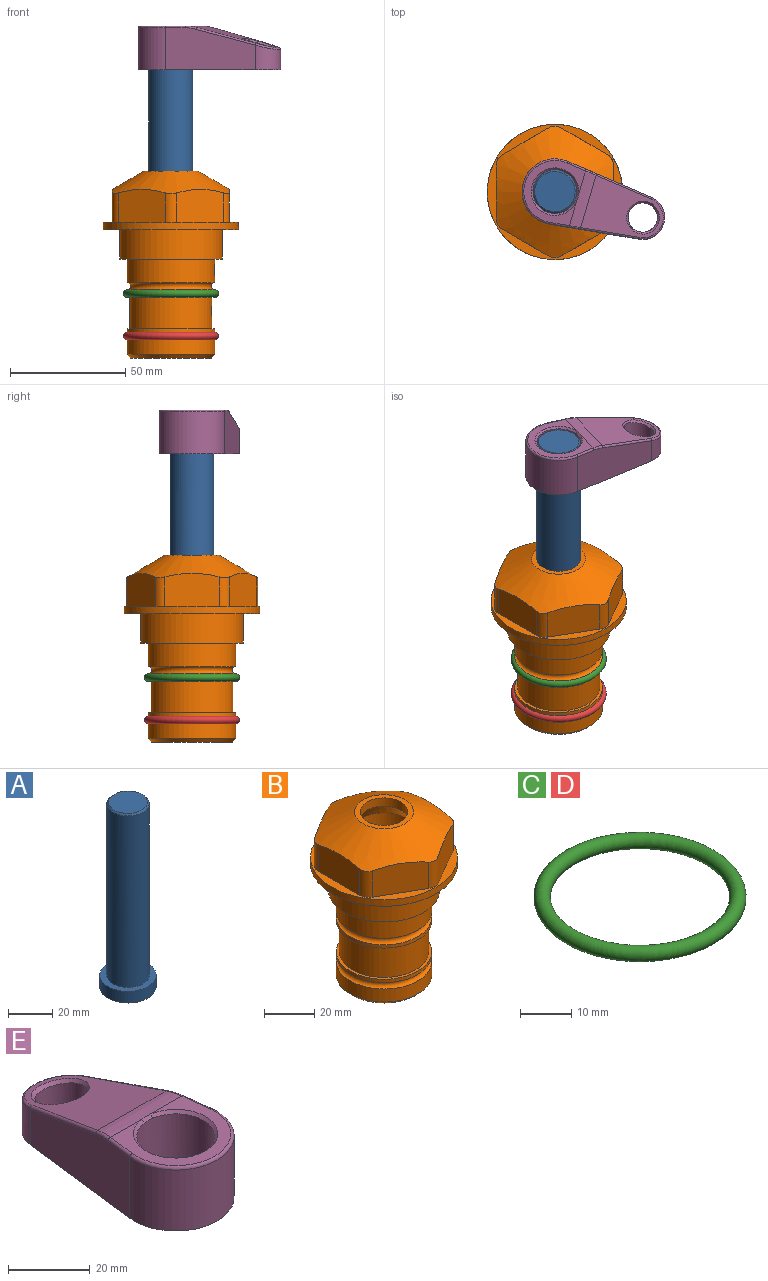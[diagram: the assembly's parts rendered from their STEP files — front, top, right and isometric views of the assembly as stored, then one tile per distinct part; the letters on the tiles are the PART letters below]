
ASSEMBLY  parts=5 mates=4
PART A: 6 faces, bbox 25.4x25.4x101.6 mm
  f0: plane 17.46x17.46mm, normal (0,0,1), area 239.5mm2, adj f5
  f1: plane 25.4x25.4mm, normal (0,0,-1), area 506.7mm2, adj f2
  f2: cylinder r=12.7mm len=25.4mm, axis (0,0,1), area 506.7mm2, adj f1,f3
  f3: plane 25.4x25.4mm, normal (0,0,1), area 221.7mm2, adj f2,f4
  f4: cylinder r=9.53mm len=94.46mm, axis (0,0,1), area 5653mm2, adj f3,f5
  f5: cone r=8.73mm half-angle=45deg, axis (0,0,-1), area 64.4mm2, adj f0,f4
PART B: 36 faces, bbox 58.7x58.7x81 mm
  f0: cylinder r=17.78mm len=35.56mm, axis (0,0,1), area 1670.8mm2, adj f23,f24,f31
  f1: cylinder r=19.05mm len=38.1mm, axis (0,0,1), area 1191.9mm2, adj f26,f27,f30
  f2: plane 58.66x58.66mm, normal (0,0,-1), area 1150.6mm2, adj f3,f28
  f3: cylinder r=29.33mm len=58.66mm, axis (0,0,-1), area 585.1mm2, adj f2,f4
  f4: plane 58.66x58.66mm, normal (0,0,1), area 475.9mm2, adj f3,f5,f6,f7,f8,f9,f10,f11
  f5: plane 20.32x14.34mm, normal (-0.5,0.87,0), area 324.4mm2, adj f4,f15,f16,f17
  f6: plane 20.32x14.34mm, normal (0.5,0.87,0), area 324.4mm2, adj f4,f14,f15,f17
  f7: plane 23.48x14.34mm, normal (1,0,0), area 324.4mm2, adj f4,f13,f14,f17
  f8: plane 20.32x14.34mm, normal (0.5,-0.87,0), area 324.4mm2, adj f4,f12,f13,f17
  f9: plane 20.32x14.34mm, normal (-0.5,-0.87,0), area 324.4mm2, adj f4,f11,f12,f17
  f10: plane 23.48x14.34mm, normal (-1,0,0), area 324.4mm2, adj f4,f11,f16,f17
  f11: cylinder r=5.08mm len=12.85mm, axis (0,0,-1), area 67.2mm2, adj f4,f9,f10,f17
  f12: cylinder r=5.08mm len=12.85mm, axis (0,0,-1), area 67.2mm2, adj f4,f8,f9,f17
  f13: cylinder r=5.08mm len=12.85mm, axis (0,0,-1), area 67.2mm2, adj f4,f7,f8,f17
  f14: cylinder r=5.08mm len=12.85mm, axis (0,0,-1), area 67.2mm2, adj f4,f6,f7,f17
  f15: cylinder r=5.08mm len=12.85mm, axis (0,0,-1), area 67.2mm2, adj f4,f5,f6,f17
  f16: cylinder r=5.08mm len=12.85mm, axis (0,0,-1), area 67.2mm2, adj f4,f5,f10,f17
  f17: cone r=11.73mm half-angle=60deg, axis (0,0,-1), area 2071.8mm2, adj f5,f6,f7,f8,f9,f10,f11,f12
  f18: plane 23.46x23.46mm, normal (0,0,1), area 147.4mm2, adj f17,f35
  f19: plane 34.93x34.93mm, normal (0,0,-1), area 958mm2, adj f29
  f20: cylinder r=19.05mm len=38.1mm, axis (0,0,1), area 760.1mm2, adj f21,f29
  f21: torus R=19.05mm, axis (0,0,1), area 565.3mm2, adj f20,f22
  f22: cylinder r=19.05mm len=38.1mm, axis (0,0,1), area 190mm2, adj f21,f23
  f23: plane 38.1x38.1mm, normal (0,0,1), area 146.9mm2, adj f0,f22
  f24: plane 38.1x38.1mm, normal (0,0,-1), area 146.9mm2, adj f0,f25
  f25: cylinder r=19.05mm len=38.1mm, axis (0,0,1), area 190mm2, adj f24,f26
  f26: torus R=19.05mm, axis (0,0,1), area 565.3mm2, adj f1,f25
  f27: plane 44.45x44.45mm, normal (0,0,-1), area 411.7mm2, adj f1,f28
  f28: cylinder r=22.23mm len=44.45mm, axis (0,0,1), area 1773.5mm2, adj f2,f27
  f29: cone r=19.05mm half-angle=45deg, axis (0,0,1), area 257.5mm2, adj f19,f20
  f30: cylinder r=3.17mm len=6.75mm, axis (-1,0,0), area 128mm2, adj f1,f33
  f31: cylinder r=3.17mm len=6.35mm, axis (-1,0,0), area 102.5mm2, adj f0,f33
  f32: plane 25.4x25.4mm, normal (0,0,1), area 506.7mm2, adj f33
  f33: cylinder r=12.7mm len=66.42mm, axis (0,0,-1), area 5236.2mm2, adj f30,f31,f32,f34
  f34: cone r=9.53mm half-angle=30deg, axis (0,0,-1), area 443.4mm2, adj f33,f35
  f35: cylinder r=9.53mm len=19.05mm, axis (0,0,-1), area 240.9mm2, adj f18,f34
PART C: 1 faces, bbox 44.7x44.7x3.2 mm
  f0: torus R=19.05mm, axis (0,0,1), area 1193.9mm2
PART D: same geometry as C
PART E: 31 faces, bbox 31.7x65.5x19.8 mm
  f0: plane 39.12x18.26mm, normal (0.99,0.12,0), area 612.2mm2, adj f1,f4,f7,f11,f13,f15
  f1: cylinder r=9.53mm len=18.91mm, axis (0,0,-1), area 296.1mm2, adj f0,f2,f7,f17
  f2: plane 39.12x18.26mm, normal (-0.99,0.12,0), area 612.2mm2, adj f1,f4,f7,f12,f14,f16
  f3: cylinder r=6.35mm len=12.7mm, axis (0,0,-1), area 362.4mm2, adj f7,f18
  f4: cylinder r=14.29mm len=28.58mm, axis (0,0,-1), area 882.2mm2, adj f0,f2,f7,f10
  f5: cylinder r=9.53mm len=19.05mm, axis (0,0,-1), area 1092.6mm2, adj f7,f19,f20
  f6: plane 26.99x23.69mm, normal (0,0,1), area 216.2mm2, adj f9,f10,f11,f12,f19
  f7: plane 63.5x28.58mm, normal (0,0,-1), area 661.8mm2, adj f0,f1,f2,f3,f4,f5,f22,f23
  f8: plane 33.52x23.6mm, normal (0,0.26,0.97), area 486mm2, adj f9,f15,f16,f17,f18
  f9: cylinder r=19.05mm len=24.72mm, axis (1,0,0), area 120.4mm2, adj f6,f8,f13,f14,f20
  f10: torus R=13.49mm, axis (0,0,1), area 59mm2, adj f4,f6,f11,f12
  f11: cylinder r=0.79mm len=8.67mm, axis (0.12,-0.99,0), area 10.8mm2, adj f0,f6,f10,f13
  f12: cylinder r=0.79mm len=8.67mm, axis (0.12,0.99,0), area 10.8mm2, adj f2,f6,f10,f14
  f13: bspline ~4.95x1.42mm, area 6.1mm2, adj f0,f9,f11,f15
  f14: bspline ~4.95x1.42mm, area 6.1mm2, adj f2,f9,f12,f16
  f15: cylinder r=0.79mm len=25.95mm, axis (0.12,-0.96,0.26), area 32.9mm2, adj f0,f8,f13,f17
  f16: cylinder r=0.79mm len=25.95mm, axis (0.12,0.96,-0.26), area 32.9mm2, adj f2,f8,f14,f17
  f17: bspline ~18.91x8.38mm, area 30mm2, adj f1,f8,f15,f16
  f18: bspline ~14.29x14.29mm, area 48.3mm2, adj f3,f8
  f19: cone r=9.53mm half-angle=45deg, axis (0,0,1), area 66.5mm2, adj f5,f6,f20
  f20: bspline ~3.22x0.96mm, area 3.5mm2, adj f5,f9,f19
  f21: plane 2.75x2.72mm, normal (0,0,-1), area 2.9mm2, adj f23,f25,f28
  f22: plane 23.05x15.88mm, normal (-0.99,-0.12,0), area 323.6mm2, adj f7,f25,f26,f27,f28,f29
  f23: plane 23.05x15.88mm, normal (0.99,-0.12,0), area 323.6mm2, adj f7,f21,f25,f27,f28,f30
  f24: cylinder r=9.53mm len=10.69mm, axis (0,0,-1), area 114.7mm2, adj f7,f27,f29,f30
  f25: cylinder r=12.7mm len=20.59mm, axis (0,0,-1), area 381.1mm2, adj f7,f21,f22,f23,f26,f28
  f26: plane 2.75x2.72mm, normal (0,0,-1), area 2.9mm2, adj f22,f25,f28
  f27: plane 19.72x18.37mm, normal (0,-0.26,-0.97), area 291.8mm2, adj f22,f23,f24,f28,f29,f30
  f28: cylinder r=15.88mm len=19.92mm, axis (1,0,0), area 54.8mm2, adj f21,f22,f23,f25,f26,f27
  f29: cylinder r=1.59mm len=11mm, axis (0,0,-1), area 34.7mm2, adj f7,f22,f24,f27
  f30: cylinder r=1.59mm len=11mm, axis (0,0,-1), area 34.7mm2, adj f7,f23,f24,f27
PLACE A rot(axis=(0,0,-1),106.4deg) t=(0,0,24.06)mm
PLACE B at identity fixed
PLACE C t=(0,0,-3.18)mm
PLACE D t=(0,0,-21.59)mm
PLACE E rot(axis=(0,0,-1),106.4deg) t=(0,0,24.86)mm
MATE cylindrical A.f2 <-> B.f0  axis (0,0,-1) through (0,0,-14.04)mm
MATE fastened C.f0 <-> B.f0  axis (0,0,1) through (0,0,-27.69)mm
MATE fastened A.f2 <-> E.f4  axis (0,0,1) through (0,0,87.56)mm
MATE fastened D.f0 <-> B.f0  axis (0,0,1) through (0,0,-46.1)mm
